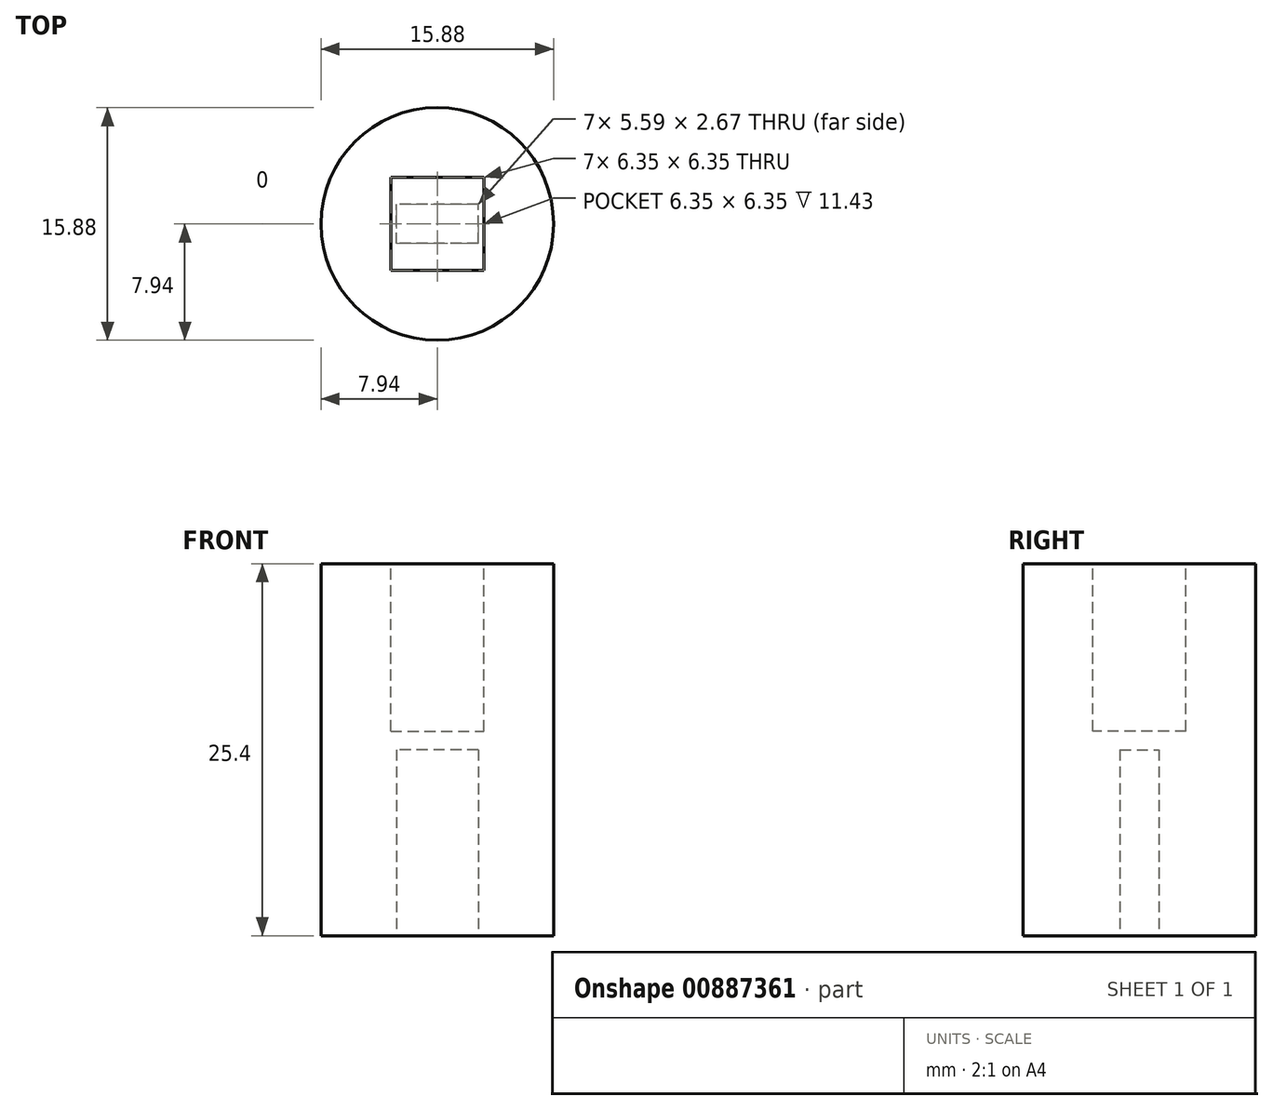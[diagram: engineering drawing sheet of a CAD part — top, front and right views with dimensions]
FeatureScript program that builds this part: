
annotation { "Feature Type Name" : "Feature", "Feature Type Description" : "" }
export const myFeature = defineFeature(function(context is Context, id is Id, definition is map)
    precondition{}
    {
        {
            var Q0;
            Q0=qCreatedBy(makeId("Top.planeOp"),FACE);
            var sketch = newSketch(context, id + "F0", { "sketchPlane" : qUnion([Q0])});
            skCircle(sketch, "E0", {"center": v(0, 0) * mm, "radius": 7.94 * mm});
            skSolve(sketch);
        }
        {
            var Q0;
            Q0=makeQuery(id+"F0.imprint","IMPRINT",FACE,{"disambiguationData":[TD([[makeQuery(id+"F0.imprint","IMPRINT",EDGE,{"derivedFrom":sQuery(id+"F0.wireOp",EDGE,"E0")}),1.0]])]});
            var Q1;
            Q1=sQuery(id+"F0.wireOp",EDGE,"E0");
            extrude(context, id + "F1", {"entities" : qUnion([Q0]), "surfaceEntities" : qUnion([Q1]), "depth" : 25.4 * mm, "offsetDistance" : 25.4 * mm});
        }
        {
            var Q0;
            Q0=makeQuery(id+"F1.opExtrude","CAP_FACE",FACE,{"disambiguationData":[OSD([sQuery(id+"F0.wireOp",EDGE,"E0")])],"isStart":false});
            var sketch = newSketch(context, id + "F2", { "sketchPlane" : qUnion([Q0])});
            skLineSegment(sketch, "E1.bottom", {"start": v(-3.18, 3.18) * mm, "end": v(3.18, 3.18) * mm});
            skLineSegment(sketch, "E1.top", {"start": v(-3.18, -3.18) * mm, "end": v(3.18, -3.18) * mm});
            skLineSegment(sketch, "E1.left", {"start": v(-3.18, 3.18) * mm, "end": v(-3.18, -3.18) * mm});
            skLineSegment(sketch, "E1.right", {"start": v(3.18, 3.18) * mm, "end": v(3.18, -3.18) * mm});
            skPoint(sketch, "E1.middle", {"position": v(0, 0) * mm});
            skSolve(sketch);
        }
        {
            var Q0;
            Q0=makeQuery(id+"F2.imprint","IMPRINT",FACE,{"disambiguationData":[TD([[makeQuery(id+"F2.imprint","IMPRINT",EDGE,{"derivedFrom":sQuery(id+"F2.wireOp",EDGE,"E1.bottom")}),-1.0]])]});
            var Q1;
            Q1=sQuery(id+"F2.wireOp",EDGE,"E1.bottom");
            extrude(context, id + "F3", {"entities" : qUnion([Q0]), "operationType" : NewBodyOperationType.REMOVE, "surfaceEntities" : qUnion([Q1]), "oppositeDirection" : true, "depth" : 11.43 * mm, "offsetDistance" : 25.4 * mm});
        }
        {
            var Q0;
            Q0=makeQuery(id+"F1.opExtrude","CAP_FACE",FACE,{"disambiguationData":[OSD([sQuery(id+"F0.wireOp",EDGE,"E0")])],"isStart":true});
            var sketch = newSketch(context, id + "F4", { "sketchPlane" : qUnion([Q0])});
            skLineSegment(sketch, "E2.bottom", {"start": v(2.8, 1.33) * mm, "end": v(-2.8, 1.33) * mm});
            skLineSegment(sketch, "E2.top", {"start": v(2.8, -1.33) * mm, "end": v(-2.8, -1.33) * mm});
            skLineSegment(sketch, "E2.left", {"start": v(2.8, 1.33) * mm, "end": v(2.8, -1.33) * mm});
            skLineSegment(sketch, "E2.right", {"start": v(-2.8, 1.33) * mm, "end": v(-2.8, -1.33) * mm});
            skPoint(sketch, "E2.middle", {"position": v(0, 0) * mm});
            skSolve(sketch);
        }
        {
            var Q0;
            Q0 = qSketchRegion(id + "F4", true);
            var Q1;
            Q1=sQuery(id+"F4.wireOp",EDGE,"E2.top");
            extrude(context, id + "F5", {"entities" : qUnion([Q0]), "operationType" : NewBodyOperationType.REMOVE, "surfaceEntities" : qUnion([Q1]), "oppositeDirection" : true, "depth" : 12.7 * mm, "offsetDistance" : 25.4 * mm});
        }
    });
